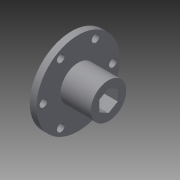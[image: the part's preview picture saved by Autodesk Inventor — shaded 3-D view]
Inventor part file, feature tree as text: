
AUTODESK INVENTOR PART (.ipt)
format: ipt  version: 2014 SP1 (Build 180222100, 222)  size: 134,656 bytes
history: native  units: in
note: dims shown in document units (in); Inventor stores cm internally (conversion verified against a paired STEP export)
features: other x1, sketch x1, imported_body x1
ambient origin geometry x8: Origin, YZ Plane, XZ Plane, XY Plane, X Axis, Y Axis, Z Axis, Center Point
bodies: Body1 (feature_tree)
feature tree (3):
  other  "500_hex_hub1"
  sketch  "Sketch1"
  imported_body  "Base1"
